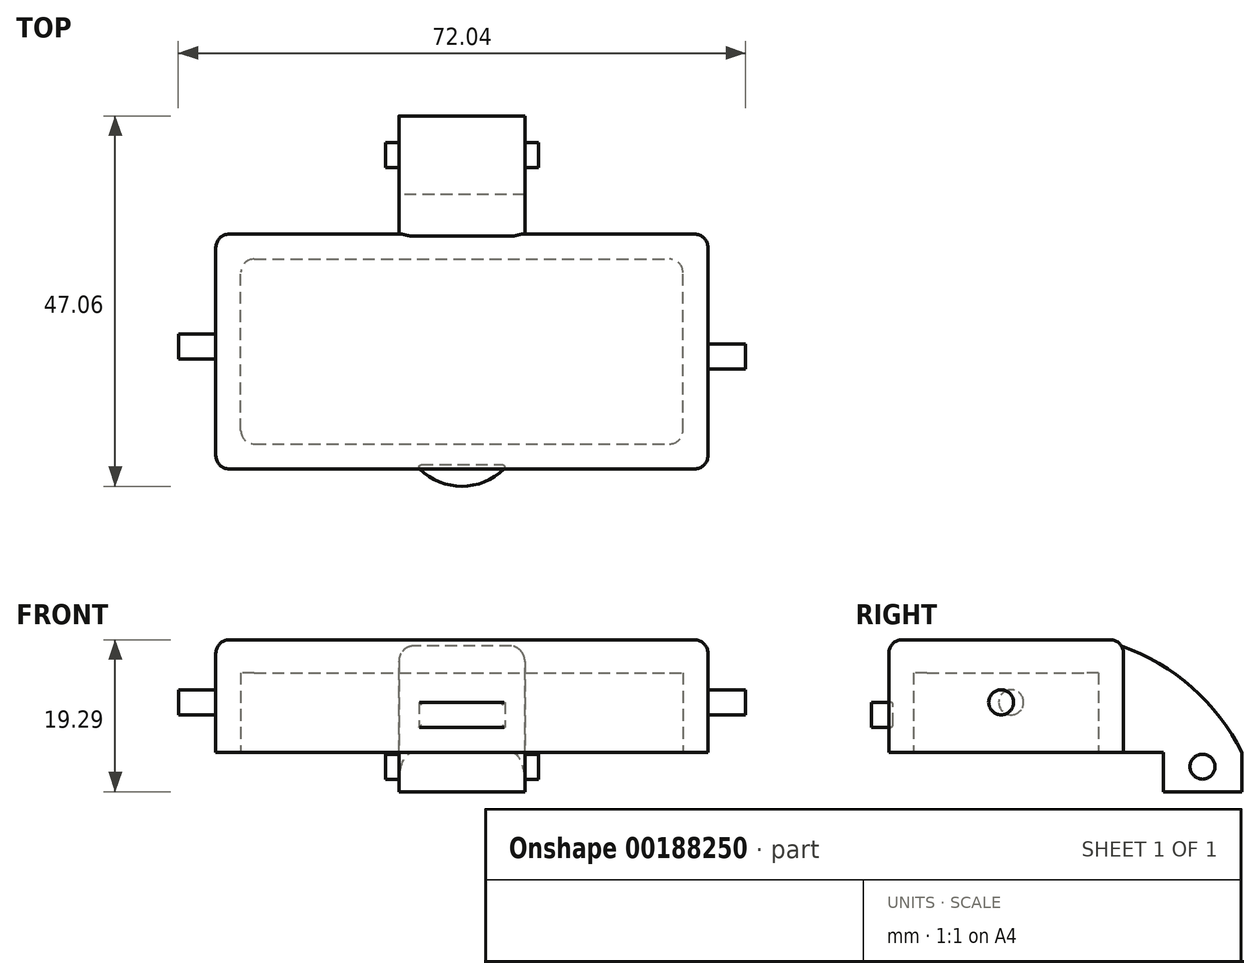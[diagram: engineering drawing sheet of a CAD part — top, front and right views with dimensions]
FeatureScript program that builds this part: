
annotation { "Feature Type Name" : "Feature", "Feature Type Description" : "" }
export const myFeature = defineFeature(function(context is Context, id is Id, definition is map)
    precondition{}
    {
        {
            var Q0;
            Q0=qCreatedBy(makeId("Top.planeOp"),FACE);
            var sketch = newSketch(context, id + "F0", { "sketchPlane" : qUnion([Q0])});
            skLineSegment(sketch, "E0.bottom", {"start": v(-31.25, 14.92) * mm, "end": v(31.25, 14.92) * mm});
            skLineSegment(sketch, "E0.top", {"start": v(-31.25, -14.92) * mm, "end": v(31.25, -14.92) * mm});
            skLineSegment(sketch, "E0.left", {"start": v(-31.25, 14.92) * mm, "end": v(-31.25, -14.92) * mm});
            skLineSegment(sketch, "E0.right", {"start": v(31.25, 14.92) * mm, "end": v(31.25, -14.92) * mm});
            skPoint(sketch, "E0.middle", {"position": v(0, 0) * mm});
            skSolve(sketch);
        }
        {
            var Q0;
            Q0 = qSketchRegion(id + "F0", true);
            extrude(context, id + "F1", {"entities" : qUnion([Q0]), "depth" : 14.29 * mm});
        }
        {
            var Q0;
            Q0=qCreatedBy(makeId("Top.planeOp"),FACE);
            cPlane(context, id + "F2", {"entities" : qUnion([Q0]), "cplaneType" : CPlaneType.OFFSET, "offset" : 3.17 * mm, "width" : 152.4 * mm, "height" : 152.4 * mm});
        }
        {
            var Q0;
            Q0=qCreatedBy(id+"F2.planeOp",FACE);
            var sketch = newSketch(context, id + "F3", { "sketchPlane" : qUnion([Q0])});
            skPoint(sketch, "E1", {"position": v(-5.85, -14.38) * mm});
            skPoint(sketch, "E2", {"position": v(5.85, -14.38) * mm});
            skArc(sketch, "E3", {"start": v(-5.85, -14.38) * mm, "mid": v(0, -17.12) * mm, "end": v(5.85, -14.38) * mm});
            skLineSegment(sketch, "E4", {"start": v(-5.85, -14.38) * mm, "end": v(5.85, -14.38) * mm});
            skSolve(sketch);
        }
        {
            var Q0;
            Q0 = qSketchRegion(id + "F3", true);
            extrude(context, id + "F4", {"entities" : qUnion([Q0]), "depth" : 3.17 * mm});
        }
        {
            var Q0;
            {var subQ0=sQuery(id+"F3.wireOp",EDGE,"E4");var subQ1=sQuery(id+"F3.wireOp",EDGE,"E3");Q0=makeQuery(id+"F4.opExtrude","SWEPT_EDGE",EDGE,{"disambiguationData":[OSD([subQ1,subQ0]),TDD([makeQuery(id+"F3.imprint","INTERSECT",VERTEX,{"disambiguationData":[OD(1.0)],"derivedFrom":[subQ1,subQ0]})])]});}
            var Q1;
            {var subQ0=sQuery(id+"F3.wireOp",EDGE,"E4");var subQ1=sQuery(id+"F3.wireOp",EDGE,"E3");Q1=makeQuery(id+"F4.opExtrude","SWEPT_EDGE",EDGE,{"disambiguationData":[OSD([subQ1,subQ0]),TDD([makeQuery(id+"F3.imprint","INTERSECT",VERTEX,{"disambiguationData":[OD(0.0)],"derivedFrom":[subQ1,subQ0]})])]});}
            var Q2;
            Q2=makeQuery(id+"F4.opExtrude","CAP_EDGE",EDGE,{"disambiguationData":[OSD([sQuery(id+"F3.wireOp",EDGE,"E4")])],"isStart":false});
            var Q3;
            Q3=makeQuery(id+"F4.opExtrude","CAP_EDGE",EDGE,{"disambiguationData":[OSD([sQuery(id+"F3.wireOp",EDGE,"E4")])],"isStart":true});
            fillet(context, id + "F5", {"entities" : qUnion([Q0, Q1, Q2, Q3]), "radius" : 0.32 * mm, "tangentPropagation" : true, "allowEdgeOverflow" : false});
        }
        {
            var Q0;
            Q0=makeQuery(id+"F1.opExtrude","SWEPT_EDGE",EDGE,{"disambiguationData":[OSD([sQuery(id+"F0.wireOp",EDGE,"E0.top"),sQuery(id+"F0.wireOp",EDGE,"E0.left")])]});
            var Q1;
            Q1=makeQuery(id+"F1.opExtrude","SWEPT_EDGE",EDGE,{"disambiguationData":[OSD([sQuery(id+"F0.wireOp",EDGE,"E0.top"),sQuery(id+"F0.wireOp",EDGE,"E0.right")])]});
            var Q2;
            Q2=makeQuery(id+"F1.opExtrude","SWEPT_EDGE",EDGE,{"disambiguationData":[OSD([sQuery(id+"F0.wireOp",EDGE,"E0.bottom"),sQuery(id+"F0.wireOp",EDGE,"E0.right")])]});
            var Q3;
            Q3=makeQuery(id+"F1.opExtrude","SWEPT_EDGE",EDGE,{"disambiguationData":[OSD([sQuery(id+"F0.wireOp",EDGE,"E0.bottom"),sQuery(id+"F0.wireOp",EDGE,"E0.left")])]});
            var Q4;
            Q4=makeQuery(id+"F1.opExtrude","CAP_FACE",FACE,{"disambiguationData":[OSD([sQuery(id+"F0.wireOp",EDGE,"E0.bottom"),sQuery(id+"F0.wireOp",EDGE,"E0.top"),sQuery(id+"F0.wireOp",EDGE,"E0.left"),sQuery(id+"F0.wireOp",EDGE,"E0.right")])],"isStart":false});
            fillet(context, id + "F6", {"entities" : qUnion([Q0, Q1, Q2, Q3, Q4]), "radius" : 1.71 * mm, "tangentPropagation" : true, "allowEdgeOverflow" : false});
        }
        {
            var Q0;
            Q0=makeQuery(id+"F1.opExtrude","CAP_FACE",FACE,{"disambiguationData":[OSD([sQuery(id+"F0.wireOp",EDGE,"E0.bottom"),sQuery(id+"F0.wireOp",EDGE,"E0.top"),sQuery(id+"F0.wireOp",EDGE,"E0.left"),sQuery(id+"F0.wireOp",EDGE,"E0.right")])],"isStart":true});
            var sketch = newSketch(context, id + "F7", { "sketchPlane" : qUnion([Q0])});
            skLineSegment(sketch, "E5.bottom", {"start": v(-28.08, 11.75) * mm, "end": v(28.08, 11.75) * mm});
            skLineSegment(sketch, "E5.top", {"start": v(-28.08, -11.75) * mm, "end": v(28.08, -11.75) * mm});
            skLineSegment(sketch, "E5.left", {"start": v(-28.08, 11.75) * mm, "end": v(-28.08, -11.75) * mm});
            skLineSegment(sketch, "E5.right", {"start": v(28.08, 11.75) * mm, "end": v(28.08, -11.75) * mm});
            skSolve(sketch);
        }
        {
            var Q0;
            Q0=makeQuery(id+"F7.imprint","IMPRINT",FACE,{"disambiguationData":[TD([[makeQuery(id+"F7.imprint","IMPRINT",EDGE,{"derivedFrom":sQuery(id+"F7.wireOp",EDGE,"E5.bottom")}),-1.0]])]});
            extrude(context, id + "F8", {"entities" : qUnion([Q0]), "operationType" : NewBodyOperationType.REMOVE, "oppositeDirection" : true, "depth" : 10.1 * mm});
        }
        {
            var Q0;
            Q0=makeQuery(id+"F8.boolean.opBoolean","COPY",EDGE,{"derivedFrom":makeQuery(id+"F8.opExtrude","SWEPT_EDGE",EDGE,{"disambiguationData":[OSD([sQuery(id+"F7.wireOp",EDGE,"E5.top"),sQuery(id+"F7.wireOp",EDGE,"E5.left")])]})});
            var Q1;
            Q1=makeQuery(id+"F8.boolean.opBoolean","COPY",EDGE,{"derivedFrom":makeQuery(id+"F8.opExtrude","SWEPT_EDGE",EDGE,{"disambiguationData":[OSD([sQuery(id+"F7.wireOp",EDGE,"E5.bottom"),sQuery(id+"F7.wireOp",EDGE,"E5.left")])]})});
            var Q2;
            Q2=makeQuery(id+"F8.boolean.opBoolean","COPY",EDGE,{"derivedFrom":makeQuery(id+"F8.opExtrude","SWEPT_EDGE",EDGE,{"disambiguationData":[OSD([sQuery(id+"F7.wireOp",EDGE,"E5.bottom"),sQuery(id+"F7.wireOp",EDGE,"E5.right")])]})});
            var Q3;
            Q3=makeQuery(id+"F8.boolean.opBoolean","COPY",EDGE,{"derivedFrom":makeQuery(id+"F8.opExtrude","SWEPT_EDGE",EDGE,{"disambiguationData":[OSD([sQuery(id+"F7.wireOp",EDGE,"E5.top"),sQuery(id+"F7.wireOp",EDGE,"E5.right")])]})});
            fillet(context, id + "F9", {"entities" : qUnion([Q0, Q1, Q2, Q3]), "radius" : 1.71 * mm, "tangentPropagation" : true, "allowEdgeOverflow" : false});
        }
        {
            var Q0;
            Q0=makeQuery(id+"F1.opExtrude","SWEPT_FACE",FACE,{"disambiguationData":[OSD([sQuery(id+"F0.wireOp",EDGE,"E0.right")])]});
            var sketch = newSketch(context, id + "F10", { "sketchPlane" : qUnion([Q0])});
            skCircle(sketch, "E6", {"center": v(-0.63, 6.35) * mm, "radius": 1.59 * mm});
            skSolve(sketch);
        }
        {
            var Q0;
            Q0=makeQuery(id+"F10.imprint","IMPRINT",FACE,{"disambiguationData":[TD([[makeQuery(id+"F10.imprint","IMPRINT",EDGE,{"derivedFrom":sQuery(id+"F10.wireOp",EDGE,"E6")}),1.0]])]});
            extrude(context, id + "F11", {"entities" : qUnion([Q0]), "operationType" : NewBodyOperationType.ADD, "depth" : 4.76 * mm});
        }
        {
            var Q0;
            Q0=makeQuery(id+"F1.opExtrude","SWEPT_FACE",FACE,{"disambiguationData":[OSD([sQuery(id+"F0.wireOp",EDGE,"E0.left")])]});
            var sketch = newSketch(context, id + "F12", { "sketchPlane" : qUnion([Q0])});
            skCircle(sketch, "E7", {"center": v(-0.63, 6.35) * mm, "radius": 1.59 * mm});
            skSolve(sketch);
        }
        {
            var Q0;
            Q0=makeQuery(id+"F12.imprint","IMPRINT",FACE,{"disambiguationData":[TD([[makeQuery(id+"F12.imprint","IMPRINT",EDGE,{"derivedFrom":sQuery(id+"F12.wireOp",EDGE,"E7")}),1.0]])]});
            extrude(context, id + "F13", {"entities" : qUnion([Q0]), "operationType" : NewBodyOperationType.ADD, "depth" : 4.76 * mm});
        }
        {
            var Q0;
            Q0=qCreatedBy(makeId("Right.planeOp"),FACE);
            var sketch = newSketch(context, id + "F14", { "sketchPlane" : qUnion([Q0])});
            skPoint(sketch, "E8", {"position": v(11.94, 14.29) * mm});
            skLineSegment(sketch, "E9", {"start": v(11.94, 0) * mm, "end": v(19.94, 0) * mm});
            skLineSegment(sketch, "E10", {"start": v(19.94, 0) * mm, "end": v(19.94, -5) * mm});
            skLineSegment(sketch, "E11", {"start": v(19.94, -5) * mm, "end": v(29.94, -5) * mm});
            skLineSegment(sketch, "E12", {"start": v(29.94, -5) * mm, "end": v(29.94, 0) * mm});
            skArc(sketch, "E13", {"start": v(29.94, 0) * mm, "mid": v(22.53, 9.15) * mm, "end": v(11.94, 14.29) * mm});
            skLineSegment(sketch, "E14", {"start": v(11.94, 14.29) * mm, "end": v(11.94, 0) * mm});
            skSolve(sketch);
        }
        {
            var Q0;
            Q0=makeQuery(id+"F14.imprint","IMPRINT",FACE,{"disambiguationData":[TD([[makeQuery(id+"F14.imprint","IMPRINT",EDGE,{"derivedFrom":sQuery(id+"F14.wireOp",EDGE,"E9")}),1.0]])]});
            extrude(context, id + "F15", {"entities" : qUnion([Q0]), "operationType" : NewBodyOperationType.ADD, "endBound" : BoundingType.SYMMETRIC, "depth" : 16 * mm});
        }
        {
            var Q0;
            Q0=makeQuery(id+"F15.opExtrude","CAP_EDGE",EDGE,{"disambiguationData":[OSD([sQuery(id+"F14.wireOp",EDGE,"E13")])],"isStart":false});
            var Q1;
            Q1=makeQuery(id+"F15.opExtrude","CAP_EDGE",EDGE,{"disambiguationData":[OSD([sQuery(id+"F14.wireOp",EDGE,"E13")])],"isStart":true});
            fillet(context, id + "F16", {"entities" : qUnion([Q0, Q1]), "radius" : 1.71 * mm, "tangentPropagation" : true, "allowEdgeOverflow" : false});
        }
        {
            var Q0;
            Q0=makeQuery(id+"F15.opExtrude","CAP_FACE",FACE,{"disambiguationData":[OSD([sQuery(id+"F14.wireOp",EDGE,"E9"),sQuery(id+"F14.wireOp",EDGE,"E10"),sQuery(id+"F14.wireOp",EDGE,"E11"),sQuery(id+"F14.wireOp",EDGE,"E12"),sQuery(id+"F14.wireOp",EDGE,"E13"),sQuery(id+"F14.wireOp",EDGE,"E14")])],"isStart":false});
            var sketch = newSketch(context, id + "F17", { "sketchPlane" : qUnion([Q0])});
            skCircle(sketch, "E15", {"center": v(24.94, -1.82) * mm, "radius": 1.59 * mm});
            skSolve(sketch);
        }
        {
            var Q0;
            Q0=makeQuery(id+"F17.imprint","IMPRINT",FACE,{"disambiguationData":[TD([[makeQuery(id+"F17.imprint","IMPRINT",EDGE,{"derivedFrom":sQuery(id+"F17.wireOp",EDGE,"E15")}),1.0]])]});
            extrude(context, id + "F18", {"entities" : qUnion([Q0]), "operationType" : NewBodyOperationType.ADD, "depth" : 1.71 * mm});
        }
        {
            var Q0;
            Q0=makeQuery(id+"F15.opExtrude","CAP_FACE",FACE,{"disambiguationData":[OSD([sQuery(id+"F14.wireOp",EDGE,"E9"),sQuery(id+"F14.wireOp",EDGE,"E10"),sQuery(id+"F14.wireOp",EDGE,"E11"),sQuery(id+"F14.wireOp",EDGE,"E12"),sQuery(id+"F14.wireOp",EDGE,"E13"),sQuery(id+"F14.wireOp",EDGE,"E14")])],"isStart":true});
            var sketch = newSketch(context, id + "F19", { "sketchPlane" : qUnion([Q0])});
            skCircle(sketch, "E16", {"center": v(-24.95, -1.82) * mm, "radius": 1.59 * mm});
            skSolve(sketch);
        }
        {
            var Q0;
            Q0 = qSketchRegion(id + "F19", true);
            extrude(context, id + "F20", {"entities" : qUnion([Q0]), "operationType" : NewBodyOperationType.ADD, "depth" : 1.71 * mm});
        }
    });
